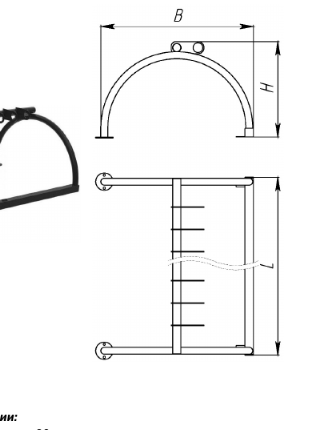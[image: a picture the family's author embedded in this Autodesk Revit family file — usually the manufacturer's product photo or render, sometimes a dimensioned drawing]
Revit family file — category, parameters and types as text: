
# Revit family: 14726 Парковка для самокатов «Юность» Хоббика
name_source: partatom
category: Антураж
revit_build: Autodesk Revit 2018 (Build: 20180423_1000(x64)
units: mm (PartAtom-declared; Revit-internal decimal feet)

## family parameters
Всегда вертикально = Да
Источник визуального образа = Геометрия семейства
На основе рабочей плоскости = Нет
Общий = Нет
При загрузке вырезать с полостями = Нет
Точка расчета площади = Нет

## types (2) — shared parameters
URL = https://hobbyka.ru
Артикул товара = Арт. 14726
Высота = 435 мм
Группа модели = Велопарковки
Изготовитель = ООО «Хоббика»
Изображение типоразмера = Парковка для самокатов «Юность» Арт 14726.jpg
Материал изделия = Сталь
Цвет каркаса = Сталь
Ширина = 700 мм

## per-type parameters (varying)
| type | 13 мест | 20 мест | Длина | Кол-во мест | Описание |
| 13 мест | Да | Нет | 1500 мм | 13 | Парковка для самокатов «Юность». Версия на 13 мест |
| 20 мест | Нет | Да | 2310 мм | 20 | Парковка для самокатов «Юность». Версия на 20 мест |
